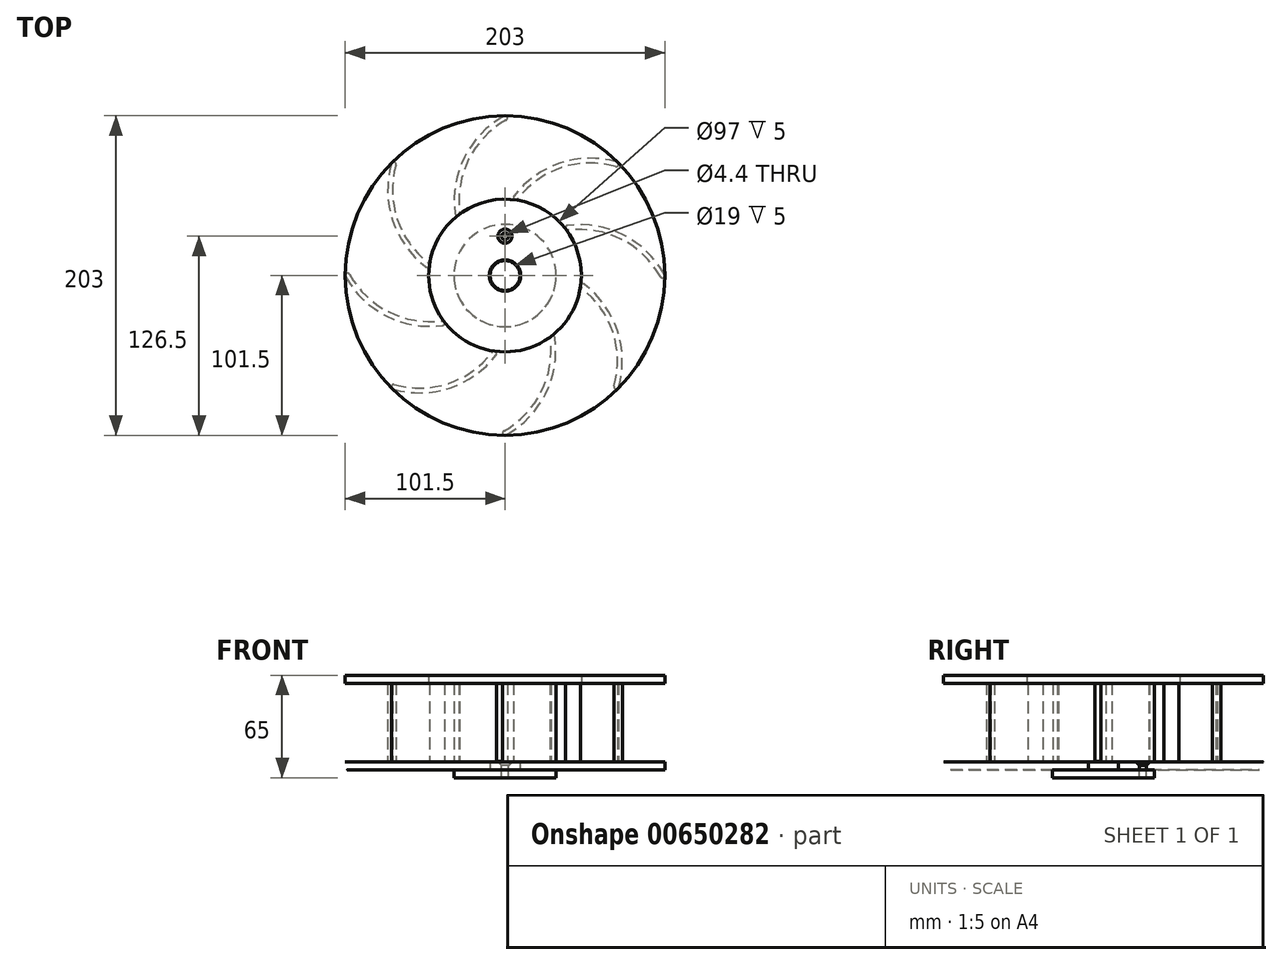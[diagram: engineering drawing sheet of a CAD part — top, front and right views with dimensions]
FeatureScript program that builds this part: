
annotation { "Feature Type Name" : "Feature", "Feature Type Description" : "" }
export const myFeature = defineFeature(function(context is Context, id is Id, definition is map)
    precondition{}
    {
        {
            var Q0;
            Q0=qCreatedBy(makeId("Top.planeOp"),FACE);
            var sketch = newSketch(context, id + "F0", { "sketchPlane" : qUnion([Q0])});
            skCircle(sketch, "E0", {"center": v(0, 0) * mm, "radius": 100 * mm, "construction": true});
            skCircle(sketch, "E1", {"center": v(0, 0) * mm, "radius": 50 * mm, "construction": true});
            skLineSegment(sketch, "E2", {"start": v(0, 102.72) * mm, "end": v(0, -110.73) * mm, "construction": true});
            skLineSegment(sketch, "E3", {"start": v(-100, 0) * mm, "end": v(126.24, 0) * mm, "construction": true});
            skLineSegment(sketch, "E4", {"start": v(0, 0) * mm, "end": v(134.34, 134.34) * mm, "construction": true});
            skLineSegment(sketch, "E5.MirrorCS", {"start": v(0, 0) * mm, "end": v(-134.34, 134.34) * mm, "construction": true});
            skLineSegment(sketch, "E6.MirrorCS", {"start": v(0, 0) * mm, "end": v(-134.34, -134.34) * mm, "construction": true});
            skLineSegment(sketch, "E7.MirrorCS", {"start": v(0, 0) * mm, "end": v(134.34, -134.34) * mm, "construction": true});
            skArc(sketch, "E8", {"start": v(70.71, 70.71) * mm, "mid": v(35.5, 69.94) * mm, "end": v(6.78, 49.54) * mm});
            skArc(sketch, "E9.0.startCap", {"start": v(71.12, 72.15) * mm, "mid": v(72.15, 70.3) * mm, "end": v(70.3, 69.27) * mm});
            skArc(sketch, "E9.0.endCap", {"start": v(7.97, 48.62) * mm, "mid": v(5.87, 48.35) * mm, "end": v(5.6, 50.45) * mm});
            skArc(sketch, "E9.0.left", {"start": v(70.3, 69.27) * mm, "mid": v(35.97, 68.51) * mm, "end": v(7.97, 48.62) * mm});
            skArc(sketch, "E9.0.right", {"start": v(71.12, 72.15) * mm, "mid": v(35.03, 71.36) * mm, "end": v(5.6, 50.45) * mm});
            skArc(sketch, "E10.1.0", {"start": v(-0.73, 101.3) * mm, "mid": v(-25.7, 75.23) * mm, "end": v(-31.72, 39.63) * mm});
            skArc(sketch, "E10.1.1", {"start": v(-28.74, 40.02) * mm, "mid": v(-30.04, 38.34) * mm, "end": v(-31.72, 39.63) * mm});
            skArc(sketch, "E10.1.2", {"start": v(0.73, 98.7) * mm, "mid": v(-23.01, 73.88) * mm, "end": v(-28.74, 40.02) * mm});
            skArc(sketch, "E10.1.3", {"start": v(-0.73, 101.3) * mm, "mid": v(1.3, 100.73) * mm, "end": v(0.73, 98.7) * mm});
            skArc(sketch, "E10.2.0", {"start": v(-72.15, 71.12) * mm, "mid": v(-71.36, 35.03) * mm, "end": v(-50.45, 5.6) * mm});
            skArc(sketch, "E10.2.1", {"start": v(-48.62, 7.97) * mm, "mid": v(-48.35, 5.87) * mm, "end": v(-50.45, 5.6) * mm});
            skArc(sketch, "E10.2.2", {"start": v(-69.27, 70.3) * mm, "mid": v(-68.51, 35.97) * mm, "end": v(-48.62, 7.97) * mm});
            skArc(sketch, "E10.2.3", {"start": v(-72.15, 71.12) * mm, "mid": v(-70.3, 72.15) * mm, "end": v(-69.27, 70.3) * mm});
            skArc(sketch, "E10.3.0", {"start": v(-101.3, -0.73) * mm, "mid": v(-75.23, -25.7) * mm, "end": v(-39.63, -31.72) * mm});
            skArc(sketch, "E10.3.1", {"start": v(-40.02, -28.74) * mm, "mid": v(-38.34, -30.04) * mm, "end": v(-39.63, -31.72) * mm});
            skArc(sketch, "E10.3.2", {"start": v(-98.7, 0.73) * mm, "mid": v(-73.88, -23.01) * mm, "end": v(-40.02, -28.74) * mm});
            skArc(sketch, "E10.3.3", {"start": v(-101.3, -0.73) * mm, "mid": v(-100.73, 1.3) * mm, "end": v(-98.7, 0.73) * mm});
            skArc(sketch, "E10.4.0", {"start": v(-71.12, -72.15) * mm, "mid": v(-35.03, -71.36) * mm, "end": v(-5.6, -50.45) * mm});
            skArc(sketch, "E10.4.1", {"start": v(-7.97, -48.62) * mm, "mid": v(-5.87, -48.35) * mm, "end": v(-5.6, -50.45) * mm});
            skArc(sketch, "E10.4.2", {"start": v(-70.3, -69.27) * mm, "mid": v(-35.97, -68.51) * mm, "end": v(-7.97, -48.62) * mm});
            skArc(sketch, "E10.4.3", {"start": v(-71.12, -72.15) * mm, "mid": v(-72.15, -70.3) * mm, "end": v(-70.3, -69.27) * mm});
            skArc(sketch, "E10.5.0", {"start": v(0.73, -101.3) * mm, "mid": v(25.7, -75.23) * mm, "end": v(31.72, -39.63) * mm});
            skArc(sketch, "E10.5.1", {"start": v(28.74, -40.02) * mm, "mid": v(30.04, -38.34) * mm, "end": v(31.72, -39.63) * mm});
            skArc(sketch, "E10.5.2", {"start": v(-0.73, -98.7) * mm, "mid": v(23.01, -73.88) * mm, "end": v(28.74, -40.02) * mm});
            skArc(sketch, "E10.5.3", {"start": v(0.73, -101.3) * mm, "mid": v(-1.3, -100.73) * mm, "end": v(-0.73, -98.7) * mm});
            skArc(sketch, "E10.6.0", {"start": v(72.15, -71.12) * mm, "mid": v(71.36, -35.03) * mm, "end": v(50.45, -5.6) * mm});
            skArc(sketch, "E10.6.1", {"start": v(48.62, -7.97) * mm, "mid": v(48.35, -5.87) * mm, "end": v(50.45, -5.6) * mm});
            skArc(sketch, "E10.6.2", {"start": v(69.27, -70.3) * mm, "mid": v(68.51, -35.97) * mm, "end": v(48.62, -7.97) * mm});
            skArc(sketch, "E10.6.3", {"start": v(72.15, -71.12) * mm, "mid": v(70.3, -72.15) * mm, "end": v(69.27, -70.3) * mm});
            skArc(sketch, "E10.7.0", {"start": v(101.3, 0.73) * mm, "mid": v(75.23, 25.7) * mm, "end": v(39.63, 31.72) * mm});
            skArc(sketch, "E10.7.1", {"start": v(40.02, 28.74) * mm, "mid": v(38.34, 30.04) * mm, "end": v(39.63, 31.72) * mm});
            skArc(sketch, "E10.7.2", {"start": v(98.7, -0.73) * mm, "mid": v(73.88, 23.01) * mm, "end": v(40.02, 28.74) * mm});
            skArc(sketch, "E10.7.3", {"start": v(101.3, 0.73) * mm, "mid": v(100.73, -1.3) * mm, "end": v(98.7, -0.73) * mm});
            skCircle(sketch, "E11", {"center": v(0, 0) * mm, "radius": 101.5 * mm});
            skCircle(sketch, "E12", {"center": v(0, 0) * mm, "radius": 48.5 * mm});
            skCircle(sketch, "E13", {"center": v(0, 0) * mm, "radius": 25 * mm, "construction": true});
            skCircle(sketch, "E14", {"center": v(0, 0) * mm, "radius": 10 * mm});
            skPoint(sketch, "E15", {"position": v(0, 25) * mm});
            skSolve(sketch);
        }
        {
            var Q0;
            {var subQ1=sQuery(id+"F0.wireOp",EDGE,"E10.6.0");Q0=makeQuery(id+"F0.imprint","IMPRINT",FACE,{"disambiguationData":[TD([[makeQuery(id+"F0.imprint","IMPRINT",EDGE,{"derivedFrom":subQ1}),-1.0]])]});}
            var Q1;
            {var subQ1=sQuery(id+"F0.wireOp",EDGE,"E10.4.0");Q1=makeQuery(id+"F0.imprint","IMPRINT",FACE,{"disambiguationData":[TD([[makeQuery(id+"F0.imprint","IMPRINT",EDGE,{"derivedFrom":subQ1}),-1.0]])]});}
            var Q2;
            {var subQ1=sQuery(id+"F0.wireOp",EDGE,"E10.5.0");Q2=makeQuery(id+"F0.imprint","IMPRINT",FACE,{"disambiguationData":[TD([[makeQuery(id+"F0.imprint","IMPRINT",EDGE,{"derivedFrom":subQ1}),-1.0]])]});}
            var Q3;
            {var subQ0=sQuery(id+"F0.wireOp",EDGE,"E12");var subQ4=makeQuery(id+"F0.imprint","INTERSECT",VERTEX,{"derivedFrom":[sQuery(id+"F0.wireOp",EDGE,"E9.0.endCap"),subQ0]});Q3=makeQuery(id+"F0.imprint","IMPRINT",FACE,{"disambiguationData":[TD([[makeQuery(id+"F0.imprint","IMPRINT",EDGE,{"disambiguationData":[TD([[subQ4,1.0]])],"derivedFrom":subQ0}),1.0]])]});}
            var Q4;
            {var subQ3=sQuery(id+"F0.wireOp",EDGE,"E9.0.left");Q4=makeQuery(id+"F0.imprint","IMPRINT",FACE,{"disambiguationData":[TD([[makeQuery(id+"F0.imprint","IMPRINT",EDGE,{"derivedFrom":subQ3}),-1.0]])]});}
            var Q5;
            {var subQ2=sQuery(id+"F0.wireOp",EDGE,"E10.1.0");Q5=makeQuery(id+"F0.imprint","IMPRINT",FACE,{"disambiguationData":[TD([[makeQuery(id+"F0.imprint","IMPRINT",EDGE,{"derivedFrom":subQ2}),1.0]])]});}
            var Q6;
            {var subQ2=sQuery(id+"F0.wireOp",EDGE,"E10.2.0");Q6=makeQuery(id+"F0.imprint","IMPRINT",FACE,{"disambiguationData":[TD([[makeQuery(id+"F0.imprint","IMPRINT",EDGE,{"derivedFrom":subQ2}),1.0]])]});}
            var Q7;
            {var subQ2=sQuery(id+"F0.wireOp",EDGE,"E10.3.0");Q7=makeQuery(id+"F0.imprint","IMPRINT",FACE,{"disambiguationData":[TD([[makeQuery(id+"F0.imprint","IMPRINT",EDGE,{"derivedFrom":subQ2}),1.0]])]});}
            var Q8;
            {var subQ2=sQuery(id+"F0.wireOp",EDGE,"E10.4.0");Q8=makeQuery(id+"F0.imprint","IMPRINT",FACE,{"disambiguationData":[TD([[makeQuery(id+"F0.imprint","IMPRINT",EDGE,{"derivedFrom":subQ2}),1.0]])]});}
            var Q9;
            {var subQ2=sQuery(id+"F0.wireOp",EDGE,"E10.5.0");Q9=makeQuery(id+"F0.imprint","IMPRINT",FACE,{"disambiguationData":[TD([[makeQuery(id+"F0.imprint","IMPRINT",EDGE,{"derivedFrom":subQ2}),1.0]])]});}
            var Q10;
            {var subQ2=sQuery(id+"F0.wireOp",EDGE,"E10.6.0");Q10=makeQuery(id+"F0.imprint","IMPRINT",FACE,{"disambiguationData":[TD([[makeQuery(id+"F0.imprint","IMPRINT",EDGE,{"derivedFrom":subQ2}),1.0]])]});}
            var Q11;
            {var subQ2=sQuery(id+"F0.wireOp",EDGE,"E10.7.0");Q11=makeQuery(id+"F0.imprint","IMPRINT",FACE,{"disambiguationData":[TD([[makeQuery(id+"F0.imprint","IMPRINT",EDGE,{"derivedFrom":subQ2}),1.0]])]});}
            var Q12;
            {var subQ4=sQuery(id+"F0.wireOp",EDGE,"E9.0.right");Q12=makeQuery(id+"F0.imprint","IMPRINT",FACE,{"disambiguationData":[TD([[makeQuery(id+"F0.imprint","IMPRINT",EDGE,{"derivedFrom":subQ4}),-1.0]])]});}
            var Q13;
            {var subQ0=sQuery(id+"F0.wireOp",EDGE,"E9.0.left");Q13=makeQuery(id+"F0.imprint","IMPRINT",FACE,{"disambiguationData":[TD([[makeQuery(id+"F0.imprint","IMPRINT",EDGE,{"derivedFrom":subQ0}),1.0]])]});}
            var Q14;
            {var subQ1=sQuery(id+"F0.wireOp",EDGE,"E10.1.0");Q14=makeQuery(id+"F0.imprint","IMPRINT",FACE,{"disambiguationData":[TD([[makeQuery(id+"F0.imprint","IMPRINT",EDGE,{"derivedFrom":subQ1}),-1.0]])]});}
            var Q15;
            {var subQ1=sQuery(id+"F0.wireOp",EDGE,"E10.2.0");Q15=makeQuery(id+"F0.imprint","IMPRINT",FACE,{"disambiguationData":[TD([[makeQuery(id+"F0.imprint","IMPRINT",EDGE,{"derivedFrom":subQ1}),-1.0]])]});}
            var Q16;
            {var subQ1=sQuery(id+"F0.wireOp",EDGE,"E10.3.0");Q16=makeQuery(id+"F0.imprint","IMPRINT",FACE,{"disambiguationData":[TD([[makeQuery(id+"F0.imprint","IMPRINT",EDGE,{"derivedFrom":subQ1}),-1.0]])]});}
            extrude(context, id + "F1", {"entities" : qUnion([Q0, Q1, Q2, Q3, Q4, Q5, Q6, Q7, Q8, Q9, Q10, Q11, Q12, Q13, Q14, Q15, Q16]), "oppositeDirection" : true, "depth" : 5 * mm, "offsetDistance" : 25 * mm});
        }
        {
            var Q0;
            {var subQ2=sQuery(id+"F0.wireOp",EDGE,"E10.2.0");Q0=makeQuery(id+"F0.imprint","IMPRINT",FACE,{"disambiguationData":[TD([[makeQuery(id+"F0.imprint","IMPRINT",EDGE,{"derivedFrom":subQ2}),1.0]])]});}
            var Q1;
            {var subQ2=sQuery(id+"F0.wireOp",EDGE,"E10.1.0");Q1=makeQuery(id+"F0.imprint","IMPRINT",FACE,{"disambiguationData":[TD([[makeQuery(id+"F0.imprint","IMPRINT",EDGE,{"derivedFrom":subQ2}),1.0]])]});}
            var Q2;
            {var subQ3=sQuery(id+"F0.wireOp",EDGE,"E9.0.left");Q2=makeQuery(id+"F0.imprint","IMPRINT",FACE,{"disambiguationData":[TD([[makeQuery(id+"F0.imprint","IMPRINT",EDGE,{"derivedFrom":subQ3}),-1.0]])]});}
            var Q3;
            {var subQ2=sQuery(id+"F0.wireOp",EDGE,"E10.7.0");Q3=makeQuery(id+"F0.imprint","IMPRINT",FACE,{"disambiguationData":[TD([[makeQuery(id+"F0.imprint","IMPRINT",EDGE,{"derivedFrom":subQ2}),1.0]])]});}
            var Q4;
            {var subQ2=sQuery(id+"F0.wireOp",EDGE,"E10.6.0");Q4=makeQuery(id+"F0.imprint","IMPRINT",FACE,{"disambiguationData":[TD([[makeQuery(id+"F0.imprint","IMPRINT",EDGE,{"derivedFrom":subQ2}),1.0]])]});}
            var Q5;
            {var subQ2=sQuery(id+"F0.wireOp",EDGE,"E10.5.0");Q5=makeQuery(id+"F0.imprint","IMPRINT",FACE,{"disambiguationData":[TD([[makeQuery(id+"F0.imprint","IMPRINT",EDGE,{"derivedFrom":subQ2}),1.0]])]});}
            var Q6;
            {var subQ2=sQuery(id+"F0.wireOp",EDGE,"E10.4.0");Q6=makeQuery(id+"F0.imprint","IMPRINT",FACE,{"disambiguationData":[TD([[makeQuery(id+"F0.imprint","IMPRINT",EDGE,{"derivedFrom":subQ2}),1.0]])]});}
            var Q7;
            {var subQ2=sQuery(id+"F0.wireOp",EDGE,"E10.3.0");Q7=makeQuery(id+"F0.imprint","IMPRINT",FACE,{"disambiguationData":[TD([[makeQuery(id+"F0.imprint","IMPRINT",EDGE,{"derivedFrom":subQ2}),1.0]])]});}
            extrude(context, id + "F2", {"entities" : qUnion([Q0, Q1, Q2, Q3, Q4, Q5, Q6, Q7]), "operationType" : NewBodyOperationType.ADD, "depth" : 50 * mm, "offsetDistance" : 25 * mm});
        }
        {
            var Q0;
            Q0=makeQuery(id+"F2.opExtrude","CAP_FACE",FACE,{"disambiguationData":[OSD([sQuery(id+"F0.wireOp",EDGE,"E10.1.0"),sQuery(id+"F0.wireOp",EDGE,"E10.1.1"),sQuery(id+"F0.wireOp",EDGE,"E10.1.2"),sQuery(id+"F0.wireOp",EDGE,"E10.1.3")])],"isStart":false});
            var sketch = newSketch(context, id + "F3", { "sketchPlane" : qUnion([Q0])});
            skCircle(sketch, "E16.0", {"center": v(0, 0) * mm, "radius": 101.5 * mm});
            skCircle(sketch, "E17.0", {"center": v(0, 0) * mm, "radius": 48.5 * mm});
            skSolve(sketch);
        }
        {
            var Q0;
            Q0 = qSketchRegion(id + "F3", true);
            extrude(context, id + "F4", {"entities" : qUnion([Q0]), "operationType" : NewBodyOperationType.ADD, "depth" : 5 * mm, "offsetDistance" : 25 * mm});
        }
        {
            var Q0;
            Q0=sQuery(id+"F0.wireOp",VERTEX,"E15");
            var Q1;
            Q1=makeQuery(id+"F1.opExtrude","SWEPT_BODY",BODY,{"disambiguationData":[OSD([sQuery(id+"F0.wireOp",EDGE,"E11"),sQuery(id+"F0.wireOp",EDGE,"E14")])]});
            hole(context, id + "F5", {"style" : HoleStyle.C_SINK, "endStyle" : HoleEndStyle.BLIND, "standardTappedOrClearance" : lookupTablePath({ "standard" : "ISO", "fit" : "Normal", "size" : "M4", "type" : "Clearance" }), "standardBlindInLast" : lookupTablePath({ "fit" : "Standard", "standard" : "ISO", "size" : "M4", "type" : "Clearance" }), "holeDiameter" : 4.4 * mm, "cSinkDiameter" : 8.96 * mm, "cSinkAngle" : 90 * degree, "majorDiameter" : 4 * mm, "holeDepth" : 5.7 * mm, "isTappedThrough" : true, "tappedDepth" : 3.6 * mm, "tapClearance" : 3, "locations" : qUnion([Q0]), "scope" : qUnion([Q1])});
        }
        {
            var Q0;
            Q0=makeQuery(id+"F1.opExtrude","CAP_FACE",FACE,{"disambiguationData":[OSD([sQuery(id+"F0.wireOp",EDGE,"E11"),sQuery(id+"F0.wireOp",EDGE,"E14")])],"isStart":false});
            var sketch = newSketch(context, id + "F6", { "sketchPlane" : qUnion([Q0])});
            skPoint(sketch, "E18.0", {"position": v(0, 0) * mm});
            skCircle(sketch, "E19", {"center": v(0, 0) * mm, "radius": 32.5 * mm});
            skPoint(sketch, "E20.0", {"position": v(0, -25) * mm});
            skCircle(sketch, "E21.0", {"center": v(0, 0) * mm, "radius": 9.5 * mm});
            skSolve(sketch);
        }
        {
            var Q0;
            Q0=makeQuery(id+"F6.imprint","IMPRINT",FACE,{"disambiguationData":[TD([[makeQuery(id+"F6.imprint","IMPRINT",EDGE,{"derivedFrom":sQuery(id+"F6.wireOp",EDGE,"E19")}),1.0]])]});
            var Q1;
            Q1=makeQuery(id+"F6.imprint","IMPRINT",FACE,{"disambiguationData":[TD([[makeQuery(id+"F6.imprint","IMPRINT",EDGE,{"derivedFrom":makeQuery(id+"FaR9pe6afVBol4i_1.2.F5.hole-0.boolean.opBoolean","INTERSECT",EDGE,{"derivedFrom":[makeQuery(id+"F1.opExtrude","CAP_FACE",FACE,{"disambiguationData":[OSD([sQuery(id+"F0.wireOp",EDGE,"E11"),sQuery(id+"F0.wireOp",EDGE,"E14")])],"isStart":false}),makeQuery(id+"FaR9pe6afVBol4i_1.2.F5.hole-0.opRevolve","SWEPT_FACE",FACE,{"disambiguationData":[OSD([sQuery(id+"FaR9pe6afVBol4i_1.2.F5.hole-0.sketch.wireOp",EDGE,"core_line_2")])]})]})}),1.0]])]});
            var Q2;
            Q2=makeQuery(id+"F6.imprint","IMPRINT",FACE,{"disambiguationData":[TD([[makeQuery(id+"F6.imprint","IMPRINT",EDGE,{"derivedFrom":makeQuery(id+"FaR9pe6afVBol4i_1.3.F5.hole-0.boolean.opBoolean","INTERSECT",EDGE,{"derivedFrom":[makeQuery(id+"F1.opExtrude","CAP_FACE",FACE,{"disambiguationData":[OSD([sQuery(id+"F0.wireOp",EDGE,"E11"),sQuery(id+"F0.wireOp",EDGE,"E14")])],"isStart":false}),makeQuery(id+"FaR9pe6afVBol4i_1.3.F5.hole-0.opRevolve","SWEPT_FACE",FACE,{"disambiguationData":[OSD([sQuery(id+"FaR9pe6afVBol4i_1.3.F5.hole-0.sketch.wireOp",EDGE,"core_line_2")])]})]})}),1.0]])]});
            var Q3;
            Q3=makeQuery(id+"F6.imprint","IMPRINT",FACE,{"disambiguationData":[TD([[makeQuery(id+"F6.imprint","IMPRINT",EDGE,{"derivedFrom":makeQuery(id+"FaR9pe6afVBol4i_1.4.F5.hole-0.boolean.opBoolean","INTERSECT",EDGE,{"derivedFrom":[makeQuery(id+"F1.opExtrude","CAP_FACE",FACE,{"disambiguationData":[OSD([sQuery(id+"F0.wireOp",EDGE,"E11"),sQuery(id+"F0.wireOp",EDGE,"E14")])],"isStart":false}),makeQuery(id+"FaR9pe6afVBol4i_1.4.F5.hole-0.opRevolve","SWEPT_FACE",FACE,{"disambiguationData":[OSD([sQuery(id+"FaR9pe6afVBol4i_1.4.F5.hole-0.sketch.wireOp",EDGE,"core_line_2")])]})]})}),1.0]])]});
            var Q4;
            Q4=makeQuery(id+"F6.imprint","IMPRINT",FACE,{"disambiguationData":[TD([[makeQuery(id+"F6.imprint","IMPRINT",EDGE,{"derivedFrom":makeQuery(id+"FaR9pe6afVBol4i_1.5.F5.hole-0.boolean.opBoolean","INTERSECT",EDGE,{"derivedFrom":[makeQuery(id+"F1.opExtrude","CAP_FACE",FACE,{"disambiguationData":[OSD([sQuery(id+"F0.wireOp",EDGE,"E11"),sQuery(id+"F0.wireOp",EDGE,"E14")])],"isStart":false}),makeQuery(id+"FaR9pe6afVBol4i_1.5.F5.hole-0.opRevolve","SWEPT_FACE",FACE,{"disambiguationData":[OSD([sQuery(id+"FaR9pe6afVBol4i_1.5.F5.hole-0.sketch.wireOp",EDGE,"core_line_2")])]})]})}),1.0]])]});
            var Q5;
            Q5=makeQuery(id+"F6.imprint","IMPRINT",FACE,{"disambiguationData":[TD([[makeQuery(id+"F6.imprint","IMPRINT",EDGE,{"derivedFrom":makeQuery(id+"F5.hole-0.boolean.opBoolean","INTERSECT",EDGE,{"derivedFrom":[makeQuery(id+"F1.opExtrude","CAP_FACE",FACE,{"disambiguationData":[OSD([sQuery(id+"F0.wireOp",EDGE,"E11"),sQuery(id+"F0.wireOp",EDGE,"E14")])],"isStart":false}),makeQuery(id+"F5.hole-0.opRevolve","SWEPT_FACE",FACE,{"disambiguationData":[OSD([sQuery(id+"F5.hole-0.sketch.wireOp",EDGE,"core_line_2")])]})]})}),1.0]])]});
            var Q6;
            Q6=makeQuery(id+"F6.imprint","IMPRINT",FACE,{"disambiguationData":[TD([[makeQuery(id+"F6.imprint","IMPRINT",EDGE,{"derivedFrom":makeQuery(id+"FaR9pe6afVBol4i_1.1.F5.hole-0.boolean.opBoolean","INTERSECT",EDGE,{"derivedFrom":[makeQuery(id+"F1.opExtrude","CAP_FACE",FACE,{"disambiguationData":[OSD([sQuery(id+"F0.wireOp",EDGE,"E11"),sQuery(id+"F0.wireOp",EDGE,"E14")])],"isStart":false}),makeQuery(id+"FaR9pe6afVBol4i_1.1.F5.hole-0.opRevolve","SWEPT_FACE",FACE,{"disambiguationData":[OSD([sQuery(id+"FaR9pe6afVBol4i_1.1.F5.hole-0.sketch.wireOp",EDGE,"core_line_2")])]})]})}),1.0]])]});
            var Q7;
            Q7=makeQuery(id+"F6.imprint","IMPRINT",FACE,{"disambiguationData":[TD([[makeQuery(id+"F6.imprint","IMPRINT",EDGE,{"derivedFrom":sQuery(id+"F6.wireOp",EDGE,"E21.0")}),-1.0]])]});
            var Q8;
            Q8=makeQuery(id+"F6.imprint","IMPRINT",FACE,{"disambiguationData":[TD([[makeQuery(id+"F6.imprint","IMPRINT",EDGE,{"derivedFrom":sQuery(id+"F6.wireOp",EDGE,"E21.0")}),1.0]])]});
            extrude(context, id + "F7", {"entities" : qUnion([Q0, Q1, Q2, Q3, Q4, Q5, Q6, Q7, Q8]), "depth" : 5 * mm, "offsetDistance" : 25 * mm});
        }
        {
            var Q0;
            Q0=sQuery(id+"F0.wireOp",VERTEX,"E15");
            var Q1;
            Q1=makeQuery(id+"F7.opExtrude","SWEPT_BODY",BODY,{"disambiguationData":[OSD([sQuery(id+"F6.wireOp",EDGE,"E19")])]});
            hole(context, id + "F8", {"style" : HoleStyle.SIMPLE, "endStyle" : HoleEndStyle.THROUGH, "standardTappedOrClearance" : lookupTablePath({ "standard" : "ISO", "engagement" : "75%", "pitch" : "0.7 mm", "size" : "M4", "type" : "Tapped" }), "standardBlindInLast" : lookupTablePath({ "standard" : "ISO", "engagement" : "75%", "pitch" : "0.7 mm", "size" : "M4", "type" : "Tapped" }), "holeDiameter" : 3.3 * mm, "majorDiameter" : 4 * mm, "showTappedDepth" : true, "isTappedThrough" : true, "tappedDepth" : 3.6 * mm, "tapClearance" : 3, "locations" : qUnion([Q0]), "scope" : qUnion([Q1])});
        }
        {
            var Q0;
            Q0=makeQuery(id+"F6.imprint","IMPRINT",FACE,{"disambiguationData":[TD([[makeQuery(id+"F6.imprint","IMPRINT",EDGE,{"derivedFrom":sQuery(id+"F6.wireOp",EDGE,"E21.0")}),-1.0]])]});
            extrude(context, id + "F9", {"entities" : qUnion([Q0]), "operationType" : NewBodyOperationType.ADD, "oppositeDirection" : true, "depth" : 10 * mm, "offsetDistance" : 25 * mm});
        }
        {
            var Q0;
            Q0=makeQuery(id+"F9.opExtrude","CAP_EDGE",EDGE,{"disambiguationData":[OSD([sQuery(id+"F6.wireOp",EDGE,"E21.0")])],"isStart":false});
            chamfer(context, id + "F10", {"entities" : qUnion([Q0]), "width" : 5 * mm, "tangentPropagation" : true});
        }
    });
